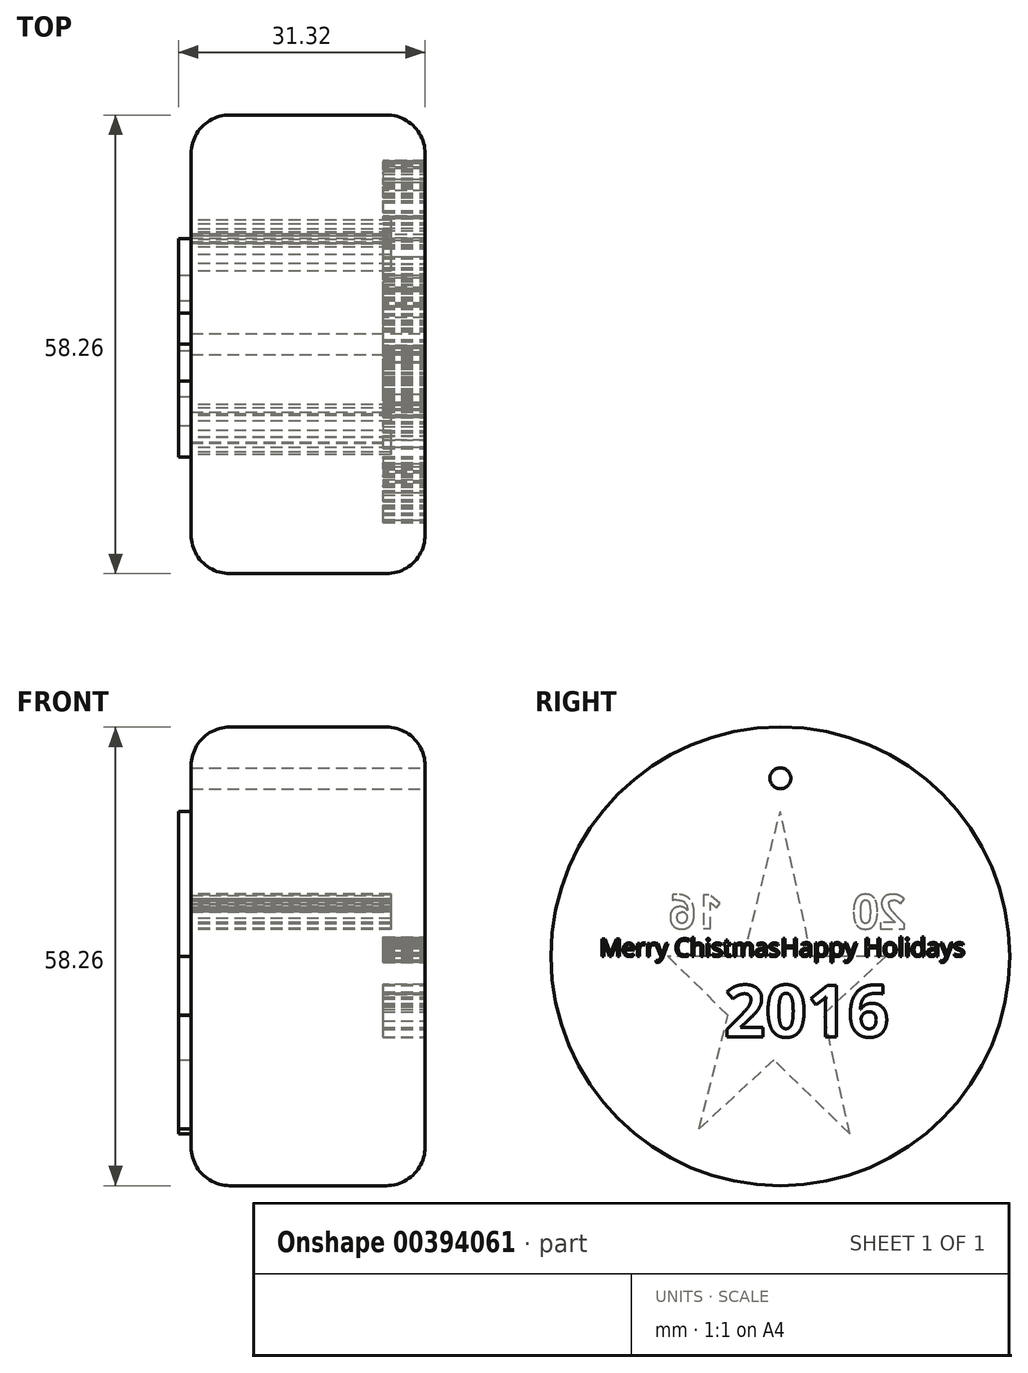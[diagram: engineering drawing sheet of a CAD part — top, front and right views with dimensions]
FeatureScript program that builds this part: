
annotation { "Feature Type Name" : "Feature", "Feature Type Description" : "" }
export const myFeature = defineFeature(function(context is Context, id is Id, definition is map)
    precondition{}
    {
        {
            var Q0;
            Q0=qCreatedBy(makeId("Right.planeOp"),FACE);
            var sketch = newSketch(context, id + "F0", { "sketchPlane" : qUnion([Q0])});
            skCircle(sketch, "E0", {"center": v(0, 0) * mm, "radius": 29.13 * mm});
            skSolve(sketch);
        }
        {
            var Q0;
            Q0=makeQuery(id+"F0.imprint","IMPRINT",FACE,{"disambiguationData":[TD([[makeQuery(id+"F0.imprint","IMPRINT",EDGE,{"derivedFrom":sQuery(id+"F0.wireOp",EDGE,"E0")}),1.0]])]});
            extrude(context, id + "F1", {"entities" : qUnion([Q0]), "oppositeDirection" : true, "depth" : 29.72 * mm});
        }
        {
            var Q0;
            Q0=makeQuery(id+"F1.opExtrude","CAP_FACE",FACE,{"disambiguationData":[OSD([sQuery(id+"F0.wireOp",EDGE,"E0")])],"isStart":true});
            var Q1;
            Q1=makeQuery(id+"F1.opExtrude","SWEPT_FACE",FACE,{"disambiguationData":[OSD([sQuery(id+"F0.wireOp",EDGE,"E0")])]});
            fillet(context, id + "F2", {"entities" : qUnion([Q0, Q1]), "radius" : 4.9 * mm, "tangentPropagation" : true, "allowEdgeOverflow" : false});
        }
        {
            var Q0;
            Q0=makeQuery(id+"F1.opExtrude","CAP_FACE",FACE,{"disambiguationData":[OSD([sQuery(id+"F0.wireOp",EDGE,"E0")])],"isStart":false});
            var sketch = newSketch(context, id + "F3", { "sketchPlane" : qUnion([Q0])});
            skLineSegment(sketch, "E1", {"start": v(10.32, -21.91) * mm, "end": v(0, 18.38) * mm});
            skLineSegment(sketch, "E2", {"start": v(-8.81, -22.56) * mm, "end": v(0, 18.38) * mm});
            skLineSegment(sketch, "E3", {"start": v(10.32, -21.91) * mm, "end": v(-13.43, 0) * mm});
            skLineSegment(sketch, "E4", {"start": v(-8.81, -22.56) * mm, "end": v(14.33, 0) * mm});
            skLineSegment(sketch, "E5", {"start": v(-13.43, 0) * mm, "end": v(14.33, 0) * mm});
            skSolve(sketch);
        }
        {
            var Q0;
            Q0=makeQuery(id+"F1.opExtrude","CAP_FACE",FACE,{"disambiguationData":[OSD([sQuery(id+"F0.wireOp",EDGE,"E0")])],"isStart":true});
            var sketch = newSketch(context, id + "F4", { "sketchPlane" : qUnion([Q0])});
            skText(sketch, "E6", { "text": "Merry Chistmas", "fontName": "OpenSans-Regular.ttf"});
            skText(sketch, "E7", { "text": "Happy Holidays", "fontName": "OpenSans-Regular.ttf"});
            skText(sketch, "E8", { "text": "2016", "fontName": "OpenSans-Bold.ttf"});
            const initialGuessF4  = {"E6": [-0.02297, 0, 1, 0, 0.00225], "E7": [0, 0, 1, 0, 0.00232], "E8": [-0.00713, -0.01022, 1, 0, 0.0066]};
            skSetInitialGuess(sketch, initialGuessF4);
            skSolve(sketch);
        }
        {
            var Q0;
            Q0 = qSketchRegion(id + "F4", true);
            extrude(context, id + "F5", {"entities" : qUnion([Q0]), "operationType" : NewBodyOperationType.REMOVE, "oppositeDirection" : true, "depth" : 5.33 * mm});
        }
        {
            var Q0;
            {var subQ0=sQuery(id+"F0.wireOp",EDGE,"E0");Q0=makeQuery(id+"F5.boolean.opBoolean","SPLIT",FACE,{"disambiguationData":[TD([makeQuery(id+"F5.opExtrude","SWEPT_FACE",FACE,{"disambiguationData":[OSD([sQuery(id+"F4.wireOp",EDGE,"E6.sketch_text.stroke-0")])]})])],"derivedFrom":makeQuery(id+"F1.opExtrude","CAP_FACE",FACE,{"disambiguationData":[OSD([subQ0])],"isStart":true})});}
            var sketch = newSketch(context, id + "F6", { "sketchPlane" : qUnion([Q0])});
            skCircle(sketch, "E9", {"center": v(0, 22.62) * mm, "radius": 1.33 * mm});
            skSolve(sketch);
        }
        {
            var Q0;
            Q0=makeQuery(id+"F6.imprint","IMPRINT",FACE,{"disambiguationData":[TD([[makeQuery(id+"F6.imprint","IMPRINT",EDGE,{"derivedFrom":sQuery(id+"F6.wireOp",EDGE,"E9")}),1.0]])]});
            extrude(context, id + "F7", {"entities" : qUnion([Q0]), "operationType" : NewBodyOperationType.REMOVE, "endBound" : BoundingType.THROUGH_ALL, "oppositeDirection" : true, "depth" : 25.4 * mm});
        }
        {
            var Q0;
            {var subQ0=sQuery(id+"F3.wireOp",EDGE,"E2");var subQ1=sQuery(id+"F3.wireOp",EDGE,"E1");var subQ2=makeQuery(id+"F3.imprint","INTERSECT",VERTEX,{"derivedFrom":[subQ1,subQ0]});Q0=makeQuery(id+"F3.imprint","IMPRINT",FACE,{"disambiguationData":[TD([[makeQuery(id+"F3.imprint","IMPRINT",EDGE,{"disambiguationData":[TD([[subQ2,1.0]])],"derivedFrom":subQ1}),1.0]])]});}
            var Q1;
            {var subQ0=sQuery(id+"F3.wireOp",EDGE,"E3");var subQ1=sQuery(id+"F3.wireOp",EDGE,"E2");var subQ2=makeQuery(id+"F3.imprint","INTERSECT",VERTEX,{"derivedFrom":[subQ1,subQ0]});Q1=makeQuery(id+"F3.imprint","IMPRINT",FACE,{"disambiguationData":[TD([[makeQuery(id+"F3.imprint","IMPRINT",EDGE,{"disambiguationData":[TD([[subQ2,-1.0]])],"derivedFrom":subQ1}),1.0]])]});}
            var Q2;
            {var subQ0=sQuery(id+"F3.wireOp",EDGE,"E4");var subQ1=sQuery(id+"F3.wireOp",EDGE,"E1");var subQ2=makeQuery(id+"F3.imprint","INTERSECT",VERTEX,{"derivedFrom":[subQ1,subQ0]});Q2=makeQuery(id+"F3.imprint","IMPRINT",FACE,{"disambiguationData":[TD([[makeQuery(id+"F3.imprint","IMPRINT",EDGE,{"disambiguationData":[TD([[subQ2,-1.0]])],"derivedFrom":subQ1}),1.0]])]});}
            var Q3;
            {var subQ1=sQuery(id+"F3.wireOp",EDGE,"E2");var subQ4=sQuery(id+"F3.wireOp",EDGE,"E3");var subQ5=makeQuery(id+"F3.imprint","INTERSECT",VERTEX,{"derivedFrom":[subQ1,subQ4]});Q3=makeQuery(id+"F3.imprint","IMPRINT",FACE,{"disambiguationData":[TD([[makeQuery(id+"F3.imprint","IMPRINT",EDGE,{"disambiguationData":[TD([[subQ5,1.0]])],"derivedFrom":subQ4}),1.0]])]});}
            var Q4;
            {var subQ1=sQuery(id+"F3.wireOp",EDGE,"E1");var subQ4=sQuery(id+"F3.wireOp",EDGE,"E4");var subQ5=makeQuery(id+"F3.imprint","INTERSECT",VERTEX,{"derivedFrom":[subQ1,subQ4]});Q4=makeQuery(id+"F3.imprint","IMPRINT",FACE,{"disambiguationData":[TD([[makeQuery(id+"F3.imprint","IMPRINT",EDGE,{"disambiguationData":[TD([[subQ5,1.0]])],"derivedFrom":subQ4}),-1.0]])]});}
            var Q5;
            {var subQ0=sQuery(id+"F3.wireOp",EDGE,"E4");var subQ1=sQuery(id+"F3.wireOp",EDGE,"E1");var subQ2=makeQuery(id+"F3.imprint","INTERSECT",VERTEX,{"derivedFrom":[subQ1,subQ0]});Q5=makeQuery(id+"F3.imprint","IMPRINT",FACE,{"disambiguationData":[TD([[makeQuery(id+"F3.imprint","IMPRINT",EDGE,{"disambiguationData":[TD([[subQ2,-1.0]])],"derivedFrom":subQ1}),-1.0]])]});}
            extrude(context, id + "F8", {"entities" : qUnion([Q0, Q1, Q2, Q3, Q4, Q5]), "operationType" : NewBodyOperationType.ADD, "depth" : 1.6 * mm});
        }
        {
            var Q0;
            {var subQ1=sQuery(id+"F3.wireOp",EDGE,"E2");var subQ9=sQuery(id+"F3.wireOp",EDGE,"E1");var subQ11=makeQuery(id+"F3.imprint","INTERSECT",VERTEX,{"derivedFrom":[subQ9,subQ1]});Q0=makeQuery(id+"F3.imprint","IMPRINT",FACE,{"disambiguationData":[TD([[makeQuery(id+"F3.imprint","IMPRINT",EDGE,{"disambiguationData":[TD([[subQ11,1.0]])],"derivedFrom":subQ9}),-1.0]])]});}
            var sketch = newSketch(context, id + "F9", { "sketchPlane" : qUnion([Q0])});
            skText(sketch, "E10", { "text": "20", "fontName": "OpenSans-Bold.ttf"});
            const initialGuessF9  = {"E10": [-0.016, 0.00351, 1, 0, 0.00436]};
            skSetInitialGuess(sketch, initialGuessF9);
            skSolve(sketch);
        }
        {
            var Q0;
            {var subQ1=sQuery(id+"F3.wireOp",EDGE,"E2");var subQ9=sQuery(id+"F3.wireOp",EDGE,"E1");var subQ11=makeQuery(id+"F3.imprint","INTERSECT",VERTEX,{"derivedFrom":[subQ9,subQ1]});Q0=makeQuery(id+"F3.imprint","IMPRINT",FACE,{"disambiguationData":[TD([[makeQuery(id+"F3.imprint","IMPRINT",EDGE,{"disambiguationData":[TD([[subQ11,1.0]])],"derivedFrom":subQ9}),-1.0]])]});}
            var sketch = newSketch(context, id + "F10", { "sketchPlane" : qUnion([Q0])});
            skText(sketch, "E11", { "text": "16", "fontName": "OpenSans-Bold.ttf"});
            const initialGuessF10  = {"E11": [0.0073, 0.00352, 1, 0, 0.00434]};
            skSetInitialGuess(sketch, initialGuessF10);
            skSolve(sketch);
        }
        {
            var Q0;
            Q0 = qSketchRegion(id + "F9", true);
            var Q1;
            Q1 = qSketchRegion(id + "F10", true);
            extrude(context, id + "F11", {"entities" : qUnion([Q0, Q1]), "operationType" : NewBodyOperationType.REMOVE, "oppositeDirection" : true, "depth" : 25.4 * mm});
        }
    });
